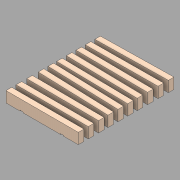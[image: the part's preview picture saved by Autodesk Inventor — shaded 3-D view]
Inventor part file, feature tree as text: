
AUTODESK INVENTOR PART (.ipt)
format: ipt  version: 2018 (Build 220112000, 112)  size: 437,248 bytes
history: native  units: mm
features: sketch x4, extrude x3
ambient origin geometry x8: Origin, YZ Plane, XZ Plane, XY Plane, X Axis, Y Axis, Z Axis, Center Point
bodies: Body1 (feature_tree)
feature tree (7):
  sketch  "Sketch5"  dims[d21=4000.0mm d22=0.0mm d23=250.0mm d24=0.0mm]
  sketch  "Sketch6"  dims[d25=500.0mm d26=0.0mm d27=26972.9mm]
  sketch  "Sketch7"  dims[d28=2103.722506mm d29=1827.15414mm]
  extrude  "Extrusion6"  Depth=250.0mm TaperAngle=0.0deg
  extrude  "Extrusion7"  Depth=26972.9mm
  extrude  "Extrusion8"  Depth=2103.722506mm
  sketch  "Sketch8"
